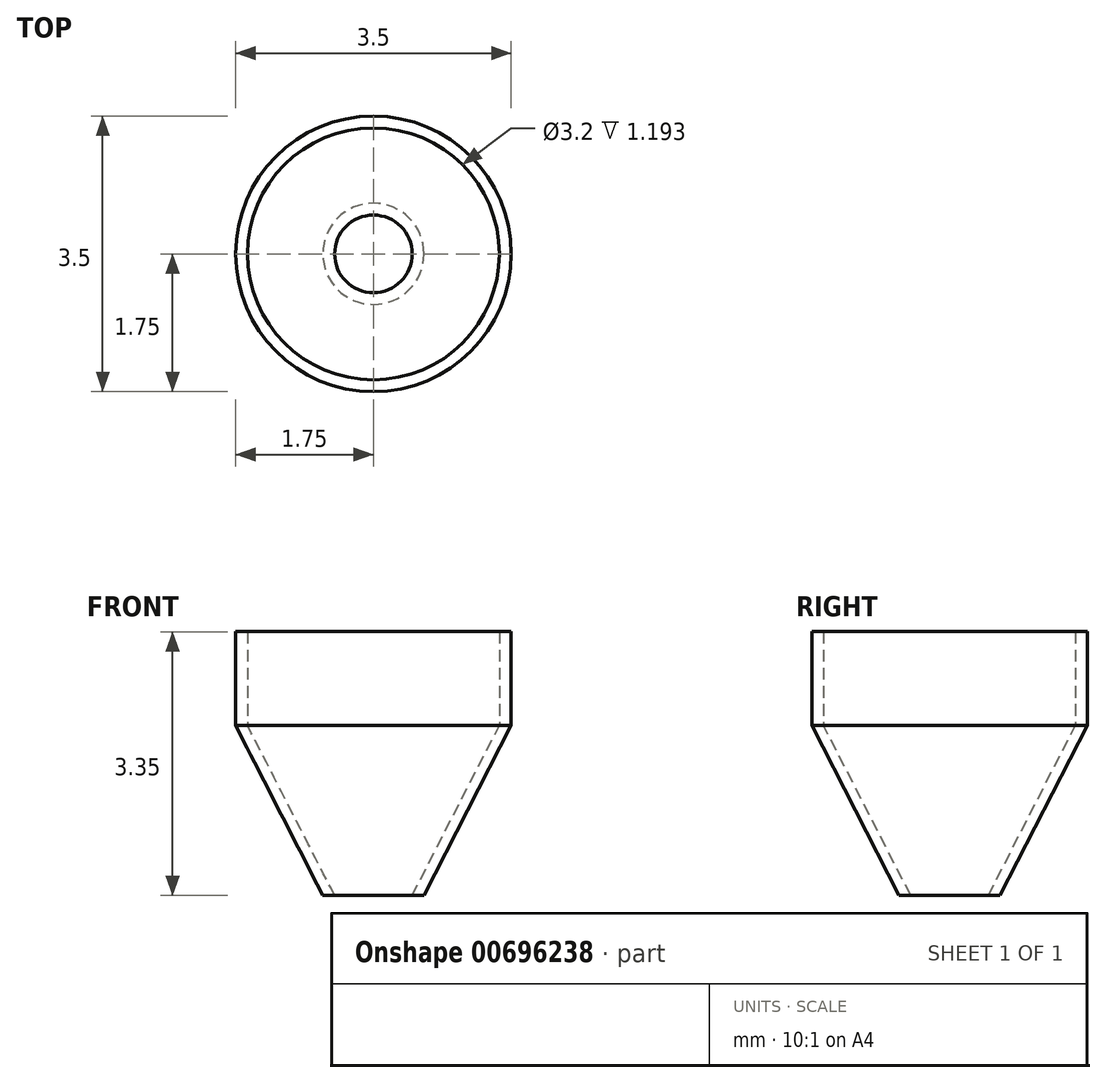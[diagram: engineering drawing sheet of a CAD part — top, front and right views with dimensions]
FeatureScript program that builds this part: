
annotation { "Feature Type Name" : "Feature", "Feature Type Description" : "" }
export const myFeature = defineFeature(function(context is Context, id is Id, definition is map)
    precondition{}
    {
        {
            var Q0;
            Q0=qCreatedBy(makeId("Front.planeOp"),FACE);
            var sketch = newSketch(context, id + "F0", { "sketchPlane" : qUnion([Q0])});
            skLineSegment(sketch, "E0", {"start": v(0, 0) * mm, "end": v(0, 3.35) * mm});
            skLineSegment(sketch, "E1", {"start": v(0, 3.35) * mm, "end": v(-1.6, 3.35) * mm});
            skLineSegment(sketch, "E2", {"start": v(-1.6, 3.35) * mm, "end": v(-1.6, 2.16) * mm});
            skLineSegment(sketch, "E3", {"start": v(-1.6, 2.16) * mm, "end": v(-0.5, 0) * mm});
            skLineSegment(sketch, "E4", {"start": v(-0.5, 0) * mm, "end": v(0, 0) * mm});
            skLineSegment(sketch, "E5", {"start": v(-1.75, 3.35) * mm, "end": v(-1.75, 2.16) * mm});
            skLineSegment(sketch, "E6", {"start": v(-1.75, 2.16) * mm, "end": v(-0.64, 0) * mm});
            skLineSegment(sketch, "E7", {"start": v(-0.64, 0) * mm, "end": v(-0.5, 0) * mm});
            skLineSegment(sketch, "E8", {"start": v(-1.75, 3.35) * mm, "end": v(-1.6, 3.35) * mm});
            skSolve(sketch);
        }
        {
            var Q0;
            Q0=makeQuery(id+"F0.imprint","IMPRINT",FACE,{"disambiguationData":[TD([[makeQuery(id+"F0.imprint","IMPRINT",EDGE,{"derivedFrom":sQuery(id+"F0.wireOp",EDGE,"E2")}),-1.0]])]});
            var Q1;
            Q1=sQuery(id+"F0.wireOp",EDGE,"E0");
            revolve(context, id + "F1", {"surfaceOperationType" : NewSurfaceOperationType.NEW, "entities" : qUnion([Q0]), "axis" : qUnion([Q1]), "revolveType" : RevolveType.FULL});
        }
        {
            var Q0;
            Q0=qCreatedBy(makeId("Top.planeOp"),FACE);
            cPlane(context, id + "F2", {"entities" : qUnion([Q0]), "cplaneType" : CPlaneType.OFFSET, "offset" : 3.71 * mm, "width" : 150 * mm, "height" : 150 * mm});
        }
        {
            var Q0;
            Q0=qCreatedBy(id+"F2.planeOp",FACE);
            var sketch = newSketch(context, id + "F3", { "sketchPlane" : qUnion([Q0])});
            skCircle(sketch, "E9", {"center": v(0, 0) * mm, "radius": 1.6 * mm});
            skSolve(sketch);
        }
        {
            var Q0;
            Q0=makeQuery(id+"F3.imprint","IMPRINT",FACE,{"disambiguationData":[TD([[makeQuery(id+"F3.imprint","IMPRINT",EDGE,{"derivedFrom":sQuery(id+"F3.wireOp",EDGE,"E9")}),1.0]])]});
            extrude(context, id + "F4", {"entities" : qUnion([Q0]), "operationType" : NewBodyOperationType.REMOVE, "flatOperationType" : FlatOperationType.REMOVE, "endBound" : BoundingType.THROUGH_ALL, "oppositeDirection" : true, "depth" : 25 * mm, "offsetDistance" : 25 * mm, "hasDraft" : true, "draftAngle" : 17 * degree, "draftPullDirection" : true, "domain" : OperationDomain.MODEL});
        }
    });
